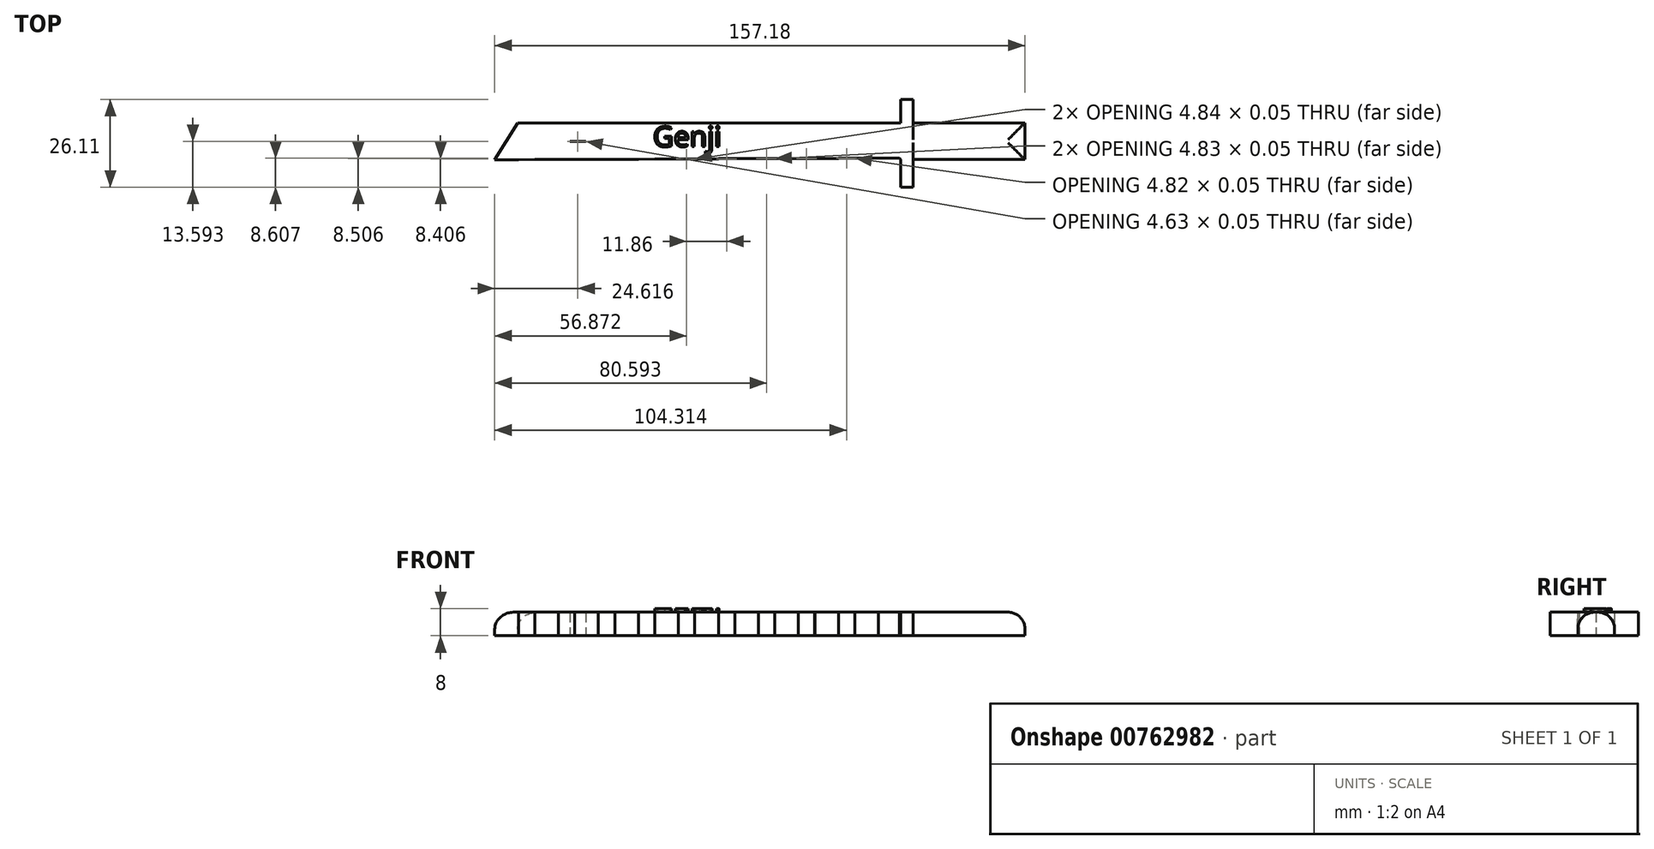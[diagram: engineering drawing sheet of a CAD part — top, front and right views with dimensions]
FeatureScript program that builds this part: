
annotation { "Feature Type Name" : "Feature", "Feature Type Description" : "" }
export const myFeature = defineFeature(function(context is Context, id is Id, definition is map)
    precondition{}
    {
        {
            var Q0;
            Q0=qCreatedBy(makeId("Top.planeOp"),FACE);
            var sketch = newSketch(context, id + "F0", { "sketchPlane" : qUnion([Q0])});
            skLineSegment(sketch, "E0", {"start": v(-59.33, 10.44) * mm, "end": v(-55.9, 15.99) * mm});
            skLineSegment(sketch, "E1", {"start": v(-55.9, 15.99) * mm, "end": v(-48.57, 15.99) * mm});
            skLineSegment(sketch, "E2", {"start": v(-48.57, 15.99) * mm, "end": v(-52.2, 10.44) * mm});
            skLineSegment(sketch, "E3", {"start": v(-52.2, 10.44) * mm, "end": v(-59.33, 10.44) * mm});
            skLineSegment(sketch, "E4.1.0.0", {"start": v(-40.4, 10.44) * mm, "end": v(-47.53, 10.44) * mm});
            skLineSegment(sketch, "E4.1.0.1", {"start": v(-44.1, 15.99) * mm, "end": v(-36.77, 15.99) * mm});
            skLineSegment(sketch, "E4.1.0.2", {"start": v(-36.77, 15.99) * mm, "end": v(-40.4, 10.44) * mm});
            skLineSegment(sketch, "E4.1.0.3", {"start": v(-47.53, 10.44) * mm, "end": v(-44.1, 15.99) * mm});
            skLineSegment(sketch, "E4.2.0.0", {"start": v(-28.6, 10.44) * mm, "end": v(-35.73, 10.44) * mm});
            skLineSegment(sketch, "E4.2.0.1", {"start": v(-32.3, 15.99) * mm, "end": v(-24.97, 15.99) * mm});
            skLineSegment(sketch, "E4.2.0.2", {"start": v(-24.97, 15.99) * mm, "end": v(-28.6, 10.44) * mm});
            skLineSegment(sketch, "E4.2.0.3", {"start": v(-35.73, 10.44) * mm, "end": v(-32.3, 15.99) * mm});
            skLineSegment(sketch, "E4.3.0.0", {"start": v(-16.8, 10.44) * mm, "end": v(-23.93, 10.44) * mm});
            skLineSegment(sketch, "E4.3.0.1", {"start": v(-20.5, 15.99) * mm, "end": v(-13.17, 15.99) * mm});
            skLineSegment(sketch, "E4.3.0.2", {"start": v(-13.17, 15.99) * mm, "end": v(-16.8, 10.44) * mm});
            skLineSegment(sketch, "E4.3.0.3", {"start": v(-23.93, 10.44) * mm, "end": v(-20.5, 15.99) * mm});
            skLineSegment(sketch, "E4.4.0.0", {"start": v(-5, 10.44) * mm, "end": v(-12.13, 10.44) * mm});
            skLineSegment(sketch, "E4.4.0.1", {"start": v(-8.7, 15.99) * mm, "end": v(-1.37, 15.99) * mm});
            skLineSegment(sketch, "E4.4.0.2", {"start": v(-1.37, 15.99) * mm, "end": v(-5, 10.44) * mm});
            skLineSegment(sketch, "E4.4.0.3", {"start": v(-12.13, 10.44) * mm, "end": v(-8.7, 15.99) * mm});
            skLineSegment(sketch, "E4.5.0.0", {"start": v(6.8, 10.44) * mm, "end": v(-0.33, 10.44) * mm});
            skLineSegment(sketch, "E4.5.0.1", {"start": v(3.1, 15.99) * mm, "end": v(10.43, 15.99) * mm});
            skLineSegment(sketch, "E4.5.0.2", {"start": v(10.43, 15.99) * mm, "end": v(6.8, 10.44) * mm});
            skLineSegment(sketch, "E4.5.0.3", {"start": v(-0.33, 10.44) * mm, "end": v(3.1, 15.99) * mm});
            skLineSegment(sketch, "E4.6.0.0", {"start": v(18.6, 10.44) * mm, "end": v(11.47, 10.44) * mm});
            skLineSegment(sketch, "E4.6.0.1", {"start": v(14.9, 15.99) * mm, "end": v(22.23, 15.99) * mm});
            skLineSegment(sketch, "E4.6.0.2", {"start": v(22.23, 15.99) * mm, "end": v(18.6, 10.44) * mm});
            skLineSegment(sketch, "E4.6.0.3", {"start": v(11.47, 10.44) * mm, "end": v(14.9, 15.99) * mm});
            skLineSegment(sketch, "E4.7.0.0", {"start": v(30.4, 10.44) * mm, "end": v(23.27, 10.44) * mm});
            skLineSegment(sketch, "E4.7.0.1", {"start": v(26.7, 15.99) * mm, "end": v(34.03, 15.99) * mm});
            skLineSegment(sketch, "E4.7.0.2", {"start": v(34.03, 15.99) * mm, "end": v(30.4, 10.44) * mm});
            skLineSegment(sketch, "E4.7.0.3", {"start": v(23.27, 10.44) * mm, "end": v(26.7, 15.99) * mm});
            skLineSegment(sketch, "E4.8.0.0", {"start": v(42.2, 10.44) * mm, "end": v(35.07, 10.44) * mm});
            skLineSegment(sketch, "E4.8.0.1", {"start": v(38.5, 15.99) * mm, "end": v(45.83, 15.99) * mm});
            skLineSegment(sketch, "E4.8.0.2", {"start": v(45.83, 15.99) * mm, "end": v(42.2, 10.44) * mm});
            skLineSegment(sketch, "E4.8.0.3", {"start": v(35.07, 10.44) * mm, "end": v(38.5, 15.99) * mm});
            skLineSegment(sketch, "E4.9.0.0", {"start": v(54, 10.44) * mm, "end": v(46.87, 10.44) * mm});
            skLineSegment(sketch, "E4.9.0.1", {"start": v(50.3, 15.99) * mm, "end": v(57.63, 15.99) * mm});
            skLineSegment(sketch, "E4.9.0.2", {"start": v(57.63, 15.99) * mm, "end": v(54, 10.44) * mm});
            skLineSegment(sketch, "E4.9.0.3", {"start": v(46.87, 10.44) * mm, "end": v(50.3, 15.99) * mm});
            skLineSegment(sketch, "E4.direction1", {"start": v(-59.33, 10.44) * mm, "end": v(-47.53, 10.44) * mm, "construction": true});
            skLineSegment(sketch, "E5", {"start": v(-52.2, 10.44) * mm, "end": v(-47.53, 10.44) * mm});
            skLineSegment(sketch, "E6", {"start": v(-40.4, 10.44) * mm, "end": v(-35.73, 10.44) * mm});
            skLineSegment(sketch, "E7", {"start": v(-28.6, 10.44) * mm, "end": v(-23.93, 10.44) * mm});
            skLineSegment(sketch, "E8", {"start": v(-16.8, 10.44) * mm, "end": v(-12.13, 10.44) * mm});
            skLineSegment(sketch, "E9", {"start": v(-5, 10.44) * mm, "end": v(-0.33, 10.44) * mm});
            skLineSegment(sketch, "E10", {"start": v(6.8, 10.44) * mm, "end": v(11.47, 10.44) * mm});
            skLineSegment(sketch, "E11", {"start": v(18.6, 10.44) * mm, "end": v(23.27, 10.44) * mm});
            skLineSegment(sketch, "E12", {"start": v(30.4, 10.44) * mm, "end": v(35.07, 10.44) * mm});
            skLineSegment(sketch, "E13", {"start": v(42.2, 10.44) * mm, "end": v(46.87, 10.44) * mm});
            skLineSegment(sketch, "E14", {"start": v(50.3, 15.99) * mm, "end": v(45.83, 15.99) * mm});
            skLineSegment(sketch, "E15", {"start": v(38.5, 15.99) * mm, "end": v(34.03, 15.99) * mm});
            skLineSegment(sketch, "E16", {"start": v(26.7, 15.99) * mm, "end": v(22.23, 15.99) * mm});
            skLineSegment(sketch, "E17", {"start": v(14.9, 15.99) * mm, "end": v(10.43, 15.99) * mm});
            skLineSegment(sketch, "E18", {"start": v(3.1, 15.99) * mm, "end": v(-1.37, 15.99) * mm});
            skLineSegment(sketch, "E19", {"start": v(-8.7, 15.99) * mm, "end": v(-13.17, 15.99) * mm});
            skLineSegment(sketch, "E20", {"start": v(-20.5, 15.99) * mm, "end": v(-24.97, 15.99) * mm});
            skLineSegment(sketch, "E21", {"start": v(-32.3, 15.99) * mm, "end": v(-36.77, 15.99) * mm});
            skLineSegment(sketch, "E22", {"start": v(-44.1, 15.99) * mm, "end": v(-48.57, 15.99) * mm});
            skLineSegment(sketch, "E23", {"start": v(57.63, 15.99) * mm, "end": v(57.63, 5.11) * mm});
            skLineSegment(sketch, "E24", {"start": v(57.63, 5.11) * mm, "end": v(54, 10.44) * mm});
            skLineSegment(sketch, "E25", {"start": v(-59.33, 10.44) * mm, "end": v(-62.66, 5.05) * mm});
            skLineSegment(sketch, "E26", {"start": v(-62.66, 5.05) * mm, "end": v(-55.66, 5.05) * mm});
            skLineSegment(sketch, "E27", {"start": v(-55.66, 5.05) * mm, "end": v(-52.2, 10.44) * mm});
            skLineSegment(sketch, "E28.1.0.0", {"start": v(-47.46, 10.49) * mm, "end": v(-50.8, 5.1) * mm});
            skLineSegment(sketch, "E28.1.0.1", {"start": v(-50.8, 5.1) * mm, "end": v(-43.8, 5.1) * mm});
            skLineSegment(sketch, "E28.1.0.2", {"start": v(-43.8, 5.1) * mm, "end": v(-40.33, 10.49) * mm});
            skLineSegment(sketch, "E28.2.0.0", {"start": v(-35.6, 10.54) * mm, "end": v(-38.94, 5.15) * mm});
            skLineSegment(sketch, "E28.2.0.1", {"start": v(-38.94, 5.15) * mm, "end": v(-31.93, 5.15) * mm});
            skLineSegment(sketch, "E28.2.0.2", {"start": v(-31.93, 5.15) * mm, "end": v(-28.47, 10.54) * mm});
            skLineSegment(sketch, "E28.3.0.0", {"start": v(-23.74, 10.59) * mm, "end": v(-27.07, 5.2) * mm});
            skLineSegment(sketch, "E28.3.0.1", {"start": v(-27.07, 5.2) * mm, "end": v(-20.07, 5.2) * mm});
            skLineSegment(sketch, "E28.3.0.2", {"start": v(-20.07, 5.2) * mm, "end": v(-16.6, 10.59) * mm});
            skLineSegment(sketch, "E28.4.0.0", {"start": v(-11.88, 10.64) * mm, "end": v(-15.21, 5.25) * mm});
            skLineSegment(sketch, "E28.4.0.1", {"start": v(-15.21, 5.25) * mm, "end": v(-8.2, 5.25) * mm});
            skLineSegment(sketch, "E28.4.0.2", {"start": v(-8.2, 5.25) * mm, "end": v(-4.74, 10.64) * mm});
            skLineSegment(sketch, "E28.5.0.0", {"start": v(-0.01, 10.69) * mm, "end": v(-3.35, 5.3) * mm});
            skLineSegment(sketch, "E28.5.0.1", {"start": v(-3.35, 5.3) * mm, "end": v(3.65, 5.3) * mm});
            skLineSegment(sketch, "E28.5.0.2", {"start": v(3.65, 5.3) * mm, "end": v(7.12, 10.69) * mm});
            skLineSegment(sketch, "E28.6.0.0", {"start": v(11.85, 10.74) * mm, "end": v(8.51, 5.35) * mm});
            skLineSegment(sketch, "E28.6.0.1", {"start": v(8.51, 5.35) * mm, "end": v(15.52, 5.35) * mm});
            skLineSegment(sketch, "E28.6.0.2", {"start": v(15.52, 5.35) * mm, "end": v(18.98, 10.74) * mm});
            skLineSegment(sketch, "E28.7.0.0", {"start": v(23.71, 10.79) * mm, "end": v(20.38, 5.4) * mm});
            skLineSegment(sketch, "E28.7.0.1", {"start": v(20.38, 5.4) * mm, "end": v(27.38, 5.4) * mm});
            skLineSegment(sketch, "E28.7.0.2", {"start": v(27.38, 5.4) * mm, "end": v(30.85, 10.79) * mm});
            skLineSegment(sketch, "E28.8.0.0", {"start": v(35.57, 10.84) * mm, "end": v(32.24, 5.45) * mm});
            skLineSegment(sketch, "E28.8.0.1", {"start": v(32.24, 5.45) * mm, "end": v(39.24, 5.45) * mm});
            skLineSegment(sketch, "E28.8.0.2", {"start": v(39.24, 5.45) * mm, "end": v(42.7, 10.84) * mm});
            skLineSegment(sketch, "E28.9.0.0", {"start": v(47.44, 10.9) * mm, "end": v(44.1, 5.5) * mm});
            skLineSegment(sketch, "E28.9.0.1", {"start": v(44.1, 5.5) * mm, "end": v(51.1, 5.5) * mm});
            skLineSegment(sketch, "E28.9.0.2", {"start": v(51.1, 5.5) * mm, "end": v(54.57, 10.9) * mm});
            skLineSegment(sketch, "E28.direction1", {"start": v(-62.66, 5.05) * mm, "end": v(-50.8, 5.1) * mm, "construction": true});
            skLineSegment(sketch, "E29", {"start": v(-55.66, 5.05) * mm, "end": v(-50.8, 5.1) * mm});
            skLineSegment(sketch, "E30.1.0.0", {"start": v(-43.8, 5.1) * mm, "end": v(-38.94, 5.15) * mm});
            skLineSegment(sketch, "E30.2.0.0", {"start": v(-31.94, 5.15) * mm, "end": v(-27.08, 5.2) * mm});
            skLineSegment(sketch, "E30.3.0.0", {"start": v(-20.08, 5.2) * mm, "end": v(-15.23, 5.25) * mm});
            skLineSegment(sketch, "E30.4.0.0", {"start": v(-8.23, 5.25) * mm, "end": v(-3.37, 5.3) * mm});
            skLineSegment(sketch, "E30.5.0.0", {"start": v(3.63, 5.3) * mm, "end": v(8.5, 5.35) * mm});
            skLineSegment(sketch, "E30.6.0.0", {"start": v(15.5, 5.35) * mm, "end": v(20.35, 5.4) * mm});
            skLineSegment(sketch, "E30.7.0.0", {"start": v(27.35, 5.4) * mm, "end": v(32.2, 5.45) * mm});
            skLineSegment(sketch, "E30.8.0.0", {"start": v(39.2, 5.45) * mm, "end": v(44.07, 5.5) * mm});
            skLineSegment(sketch, "E30.9.0.0", {"start": v(51.07, 5.5) * mm, "end": v(55.92, 5.55) * mm});
            skLineSegment(sketch, "E30.direction1", {"start": v(-55.66, 5.05) * mm, "end": v(-43.8, 5.1) * mm, "construction": true});
            skLineSegment(sketch, "E31", {"start": v(-40.33, 10.49) * mm, "end": v(-35.73, 10.44) * mm});
            skLineSegment(sketch, "E32", {"start": v(-31.93, 5.15) * mm, "end": v(-27.07, 5.2) * mm});
            skLineSegment(sketch, "E33", {"start": v(-20.07, 5.2) * mm, "end": v(-15.21, 5.25) * mm});
            skLineSegment(sketch, "E34", {"start": v(-8.2, 5.25) * mm, "end": v(-3.35, 5.3) * mm});
            skLineSegment(sketch, "E35", {"start": v(3.65, 5.3) * mm, "end": v(8.51, 5.35) * mm});
            skLineSegment(sketch, "E36", {"start": v(15.52, 5.35) * mm, "end": v(20.38, 5.4) * mm});
            skLineSegment(sketch, "E37", {"start": v(27.38, 5.4) * mm, "end": v(32.24, 5.45) * mm});
            skLineSegment(sketch, "E38", {"start": v(39.24, 5.45) * mm, "end": v(44.1, 5.5) * mm});
            skLineSegment(sketch, "E39", {"start": v(55.92, 5.55) * mm, "end": v(57.32, 5.57) * mm});
            skLineSegment(sketch, "E40.bottom", {"start": v(57.63, 15.99) * mm, "end": v(74.97, 15.99) * mm});
            skLineSegment(sketch, "E40.top", {"start": v(57.63, 5.08) * mm, "end": v(74.97, 5.08) * mm});
            skLineSegment(sketch, "E40.left", {"start": v(57.63, 15.99) * mm, "end": v(57.63, 5.08) * mm});
            skLineSegment(sketch, "E41", {"start": v(57.63, 15.99) * mm, "end": v(57.63, 22.98) * mm});
            skLineSegment(sketch, "E42", {"start": v(57.63, 22.98) * mm, "end": v(57.63, 5.11) * mm});
            skLineSegment(sketch, "E43", {"start": v(57.63, 5.08) * mm, "end": v(57.63, -3.13) * mm});
            skLineSegment(sketch, "E44", {"start": v(57.63, 22.98) * mm, "end": v(61.37, 22.98) * mm});
            skLineSegment(sketch, "E45", {"start": v(61.37, 22.98) * mm, "end": v(61.37, 15.99) * mm});
            skLineSegment(sketch, "E46", {"start": v(57.63, -3.13) * mm, "end": v(61.37, -3.13) * mm});
            skLineSegment(sketch, "E47", {"start": v(61.37, -3.13) * mm, "end": v(61.37, 5.08) * mm});
            skLineSegment(sketch, "E48", {"start": v(61.37, 15.99) * mm, "end": v(61.37, 5.08) * mm});
            skLineSegment(sketch, "E49", {"start": v(74.97, 15.99) * mm, "end": v(87.5, 15.99) * mm});
            skLineSegment(sketch, "E50", {"start": v(87.5, 5.08) * mm, "end": v(74.97, 5.08) * mm});
            skLineSegment(sketch, "E51", {"start": v(87.5, 15.99) * mm, "end": v(94.52, 15.99) * mm});
            skLineSegment(sketch, "E52", {"start": v(94.52, 15.99) * mm, "end": v(94.52, 5.08) * mm});
            skLineSegment(sketch, "E53", {"start": v(94.52, 5.08) * mm, "end": v(87.5, 5.08) * mm});
            skLineSegment(sketch, "E54", {"start": v(-62.66, 5.05) * mm, "end": v(-62.65, 2.47) * mm});
            skLineSegment(sketch, "E55", {"start": v(-62.66, 5.05) * mm, "end": v(55.92, 5.55) * mm});
            skSolve(sketch);
        }
        {
            var Q0;
            Q0 = qSketchRegion(id + "F0", true);
            extrude(context, id + "F1", {"entities" : qUnion([Q0]), "depth" : 7 * mm, "offsetDistance" : 25 * mm});
        }
        {
            var Q0;
            Q0=qCreatedBy(makeId("Top.planeOp"),FACE);
            var sketch = newSketch(context, id + "F2", { "sketchPlane" : qUnion([Q0])});
            skText(sketch, "E56", { "text": "Genji\n", "fontName": "OpenSans-Regular.ttf"});
            const initialGuessF2  = {"E56": [-0.01574, 0.00889, 1, 0, 0.00606]};
            skSetInitialGuess(sketch, initialGuessF2);
            skSolve(sketch);
        }
        {
            var Q0;
            Q0 = qSketchRegion(id + "F2", true);
            extrude(context, id + "F3", {"entities" : qUnion([Q0]), "operationType" : NewBodyOperationType.ADD, "depth" : 8 * mm, "offsetDistance" : 25 * mm});
        }
        {
            var Q0;
            Q0=makeQuery(id+"F1.opExtrude","CAP_EDGE",EDGE,{"disambiguationData":[OSD([sQuery(id+"F0.wireOp",EDGE,"E0"),sQuery(id+"F0.wireOp",EDGE,"E25")])],"isStart":false});
            var Q1;
            Q1=makeQuery(id+"F1.opExtrude","CAP_EDGE",EDGE,{"disambiguationData":[OSD([sQuery(id+"F0.wireOp",EDGE,"E52")])],"isStart":false});
            var Q2;
            Q2=makeQuery(id+"F1.opExtrude","CAP_EDGE",EDGE,{"disambiguationData":[OSD([sQuery(id+"F0.wireOp",EDGE,"E40.bottom"),sQuery(id+"F0.wireOp",EDGE,"E49"),sQuery(id+"F0.wireOp",EDGE,"E51")])],"isStart":false});
            var Q3;
            Q3=makeQuery(id+"F1.opExtrude","CAP_EDGE",EDGE,{"disambiguationData":[OSD([sQuery(id+"F0.wireOp",EDGE,"E40.top"),sQuery(id+"F0.wireOp",EDGE,"E50"),sQuery(id+"F0.wireOp",EDGE,"E53")])],"isStart":false});
            fillet(context, id + "F4", {"entities" : qUnion([Q0, Q1, Q2, Q3]), "radius" : 5 * mm, "tangentPropagation" : true, "allowEdgeOverflow" : false});
        }
    });
